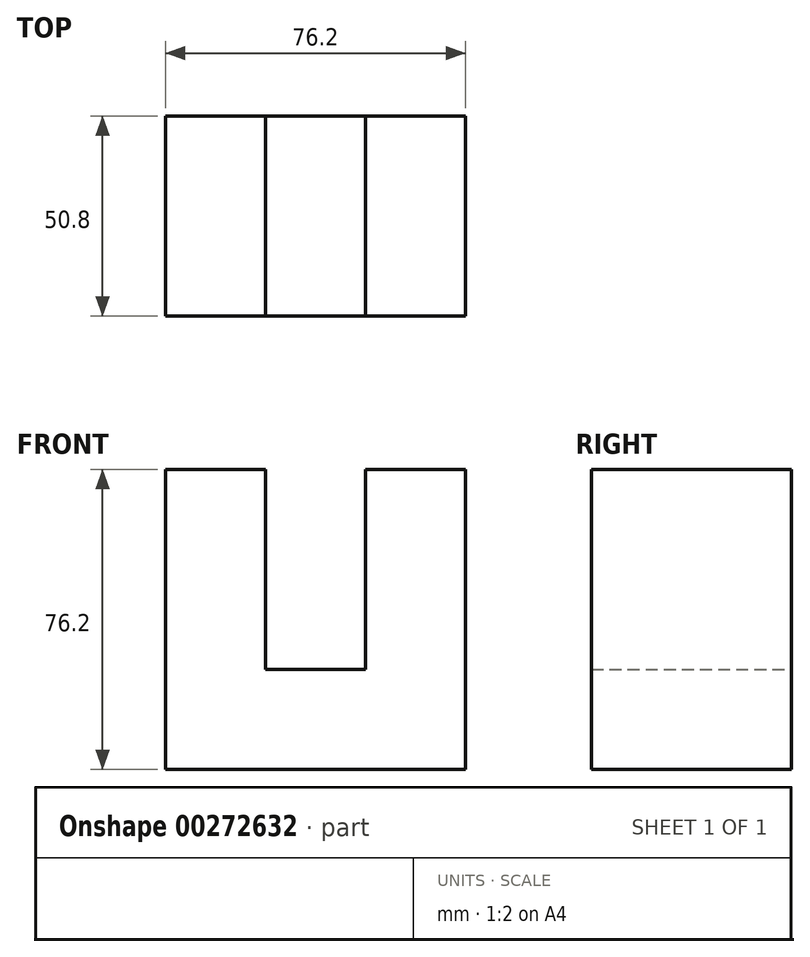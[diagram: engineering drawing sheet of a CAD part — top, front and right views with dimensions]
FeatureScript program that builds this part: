
annotation { "Feature Type Name" : "Feature", "Feature Type Description" : "" }
export const myFeature = defineFeature(function(context is Context, id is Id, definition is map)
    precondition{}
    {
        {
            var Q0;
            Q0=qCreatedBy(makeId("Front.planeOp"),FACE);
            var sketch = newSketch(context, id + "F0", { "sketchPlane" : qUnion([Q0])});
            skLineSegment(sketch, "E0", {"start": v(-47.36, 49.47) * mm, "end": v(-47.36, -26.73) * mm});
            skLineSegment(sketch, "E1", {"start": v(-47.36, -26.73) * mm, "end": v(28.84, -26.73) * mm});
            skLineSegment(sketch, "E2", {"start": v(28.84, -26.73) * mm, "end": v(28.84, 49.47) * mm});
            skLineSegment(sketch, "E3", {"start": v(28.84, 49.47) * mm, "end": v(3.44, 49.47) * mm});
            skLineSegment(sketch, "E4", {"start": v(3.44, 49.47) * mm, "end": v(3.44, -1.33) * mm});
            skLineSegment(sketch, "E5", {"start": v(3.44, -1.33) * mm, "end": v(-21.96, -1.33) * mm});
            skLineSegment(sketch, "E6", {"start": v(-21.96, -1.33) * mm, "end": v(-21.96, 49.47) * mm});
            skLineSegment(sketch, "E7", {"start": v(-47.36, 49.47) * mm, "end": v(-21.96, 49.47) * mm});
            skSolve(sketch);
        }
        {
            var Q0;
            Q0 = qSketchRegion(id + "F0", true);
            extrude(context, id + "F1", {"entities" : qUnion([Q0]), "depth" : 50.8 * mm});
        }
    });
